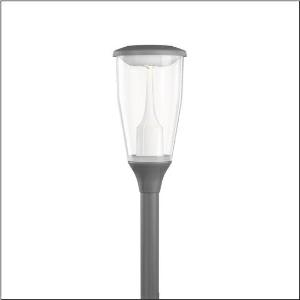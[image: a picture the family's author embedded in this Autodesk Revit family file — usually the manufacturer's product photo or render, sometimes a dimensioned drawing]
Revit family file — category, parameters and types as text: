
# Revit family: dl_11_iq___p1_0a_5xa5575ff14h000022_b904
name_source: partatom
category: Lighting Fixtures
units: mm (PartAtom-declared; Revit-internal decimal feet)

## family parameters
Cut with Voids When Loaded = No
Host = Face
Light Source = No
Part Type = Normal
Room Calculation Point = No
Round Connector Dimension = Use Diameter
Shared = No

## types (1)
- --- (1 x LED, 1530 lm, 10.5 W, 3000K)
    Apparent Load = 11 VA
    CIE Flux Codes = 34 63 91 95 100
    Color Rendering = 70
    Color Temperature = 3000K
    Default Elevation = 1800 mm
    Description = DL 11 iQ, mast luminaire, Module 540 iQ-SR, primary light control with 3 zone facetted reflector, of plastic, silver coated, highly specular, structured, primary optical cover: cover, of PMMA, transparent, light distribution: P1.0a, light emission: direct distribution, primary light characteristic: asymmetric, installation type: post-top, LED, High Power LED, rated luminous flux: 1.560lm, luminous efficacy: 149lm/W, light colour: 730, colour temperature: 3000K, control: Street-Remote, Auto-Match, Temp-Guard, Lumen-Switch, Night-Set, Smart-Wire, Light-Fading, Desk-Remote (wireless, voltage-free reading and setting of iQ features in the workshop via application-optimized NFC function/RFID function), optimised constant luminous flux control (CLO 2.0), mains connection: 220..240V, AC, 50/60Hz, connection cable pre-assembled, cable length: 5,5m, wiring characteristics: H07RN-F, 5-core, 1.5mm², start of lifetime: 10W, end of service life: 11W, reduction: 5W, luminaire housing, upper part, of diecast aluminium, coated, Siteco® metallic grey (DB 702S), spigot size: 76mm (post-top), post-top mast mounting element, of diecast aluminium, coated, Siteco® metallic grey (DB 702S), Module 540 iQ-SR, traffic white (RAL 9016), equipment: standard, protection rating (complete): IP66, insulation class (complete): insulation class II (safety insulation), certification: CE, ENEC, ENEC+, VDE, packaging unit: 1 piece

Light Distribution: P1.0a
    Height = 665 mm
    Lamp = 1 x LED
    Lamp Light Flux = 1530 lm
    Lamp Power = 10.5 W
    Lamp count = 1
    Length = 334 mm
    Luminous efficacy = 146 lm/W
    Manufacturer = Siteco
    ModVariant = No
    Model = 5XA5575FF14H000022
    Number of Poles = 1
    OnlyDefault = Yes
    Power Factor = 1
    Product Name = DL 11 iQ | P1.0a
    Product group = mast luminaire | pylon top
    ProductGroupID = 6100
    Protection Class = Protection class II
    Protection Degree = IP 66
    RLX_Detail_Level = 1
    RLX_Emergency_Light_Flux = 0 lm
    RLX_Emergency_Type = 0
    RLX_Emergency_Type_DB = No
    RlxData = <blob elided: 104317 chars, md5=bb6f7583>
    Socket = socket
    Standby Power = 0 W
    System Light Flux = 1530 lm
    System Power = 11 W
    Type Comments = factory setting: luminous flux: 100 % | dim-lin: 254 | 419 mA
    Type Image = l_1258354.jpg
    URL = http://relux.com
    VarID = @adj_060535
    Voltage = 0 V
    Weight = 0.00 kg
    Width = 0 mm  [stored 0 ft]

note: [stored X ft] marks values corroborated as IEEE doubles in the binary element streams (Revit-internal decimal feet)

## geometry (parser evidence)
native form markers: Blend x4, Sweep x10
no freeform markers — native parametric forms only
